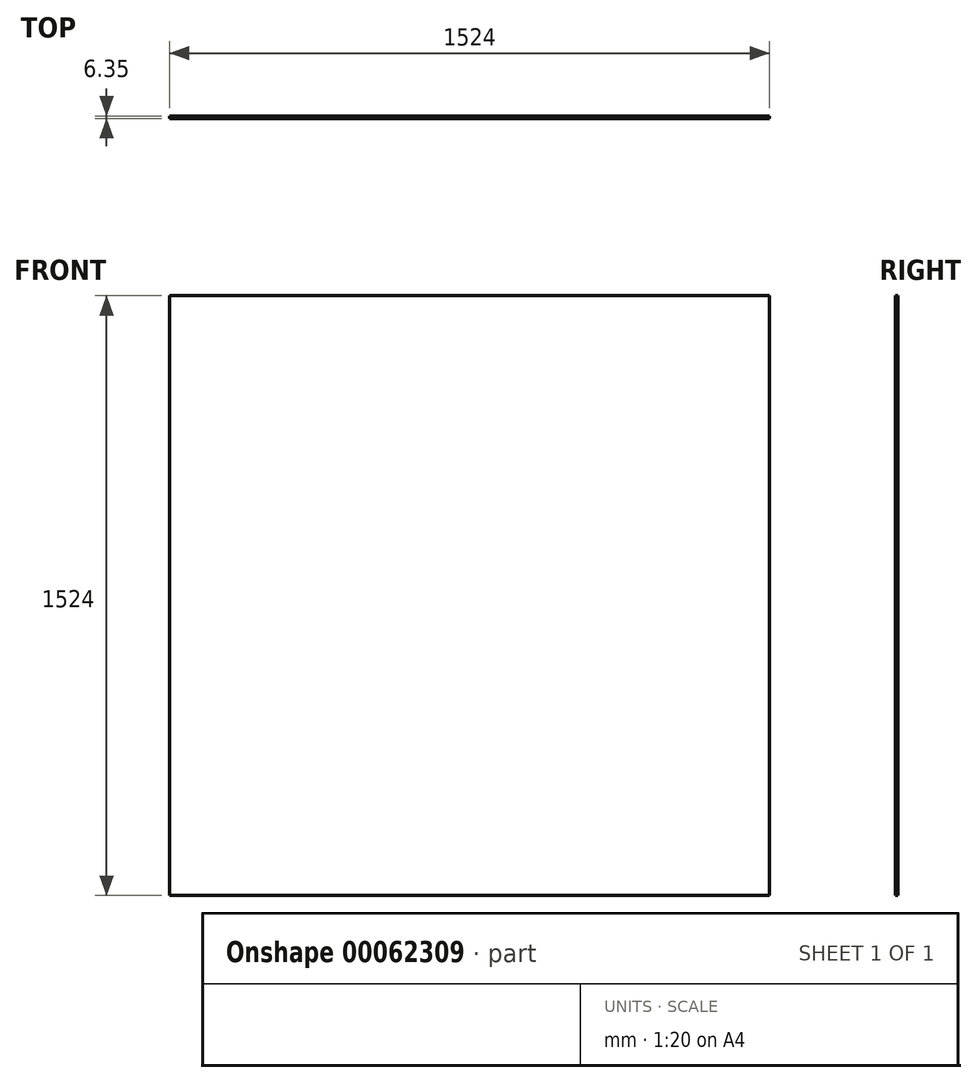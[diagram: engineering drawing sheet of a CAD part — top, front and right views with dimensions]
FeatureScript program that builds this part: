
annotation { "Feature Type Name" : "Feature", "Feature Type Description" : "" }
export const myFeature = defineFeature(function(context is Context, id is Id, definition is map)
    precondition{}
    {
        {
            var Q0;
            Q0=qCreatedBy(makeId("Front.planeOp"),FACE);
            var sketch = newSketch(context, id + "F0", { "sketchPlane" : qUnion([Q0])});
            skLineSegment(sketch, "E0.rect.bottom", {"start": v(762, 762) * mm, "end": v(-762, 762) * mm});
            skLineSegment(sketch, "E0.rect.top", {"start": v(762, -762) * mm, "end": v(-762, -762) * mm});
            skLineSegment(sketch, "E0.rect.left", {"start": v(762, 762) * mm, "end": v(762, -762) * mm});
            skLineSegment(sketch, "E0.rect.right", {"start": v(-762, 762) * mm, "end": v(-762, -762) * mm});
            skPoint(sketch, "E0.rect.middle", {"position": v(0, 0) * mm});
            skSolve(sketch);
        }
        {
            var Q0;
            Q0=makeQuery(id+"F0.imprint","IMPRINT",FACE,{"disambiguationData":[TD([[makeQuery(id+"F0.imprint","IMPRINT",EDGE,{"derivedFrom":sQuery(id+"F0.wireOp",EDGE,"E0.rect.bottom")}),1.0]])]});
            extrude(context, id + "F1", {"entities" : qUnion([Q0]), "depth" : 6.35 * mm});
        }
    });
